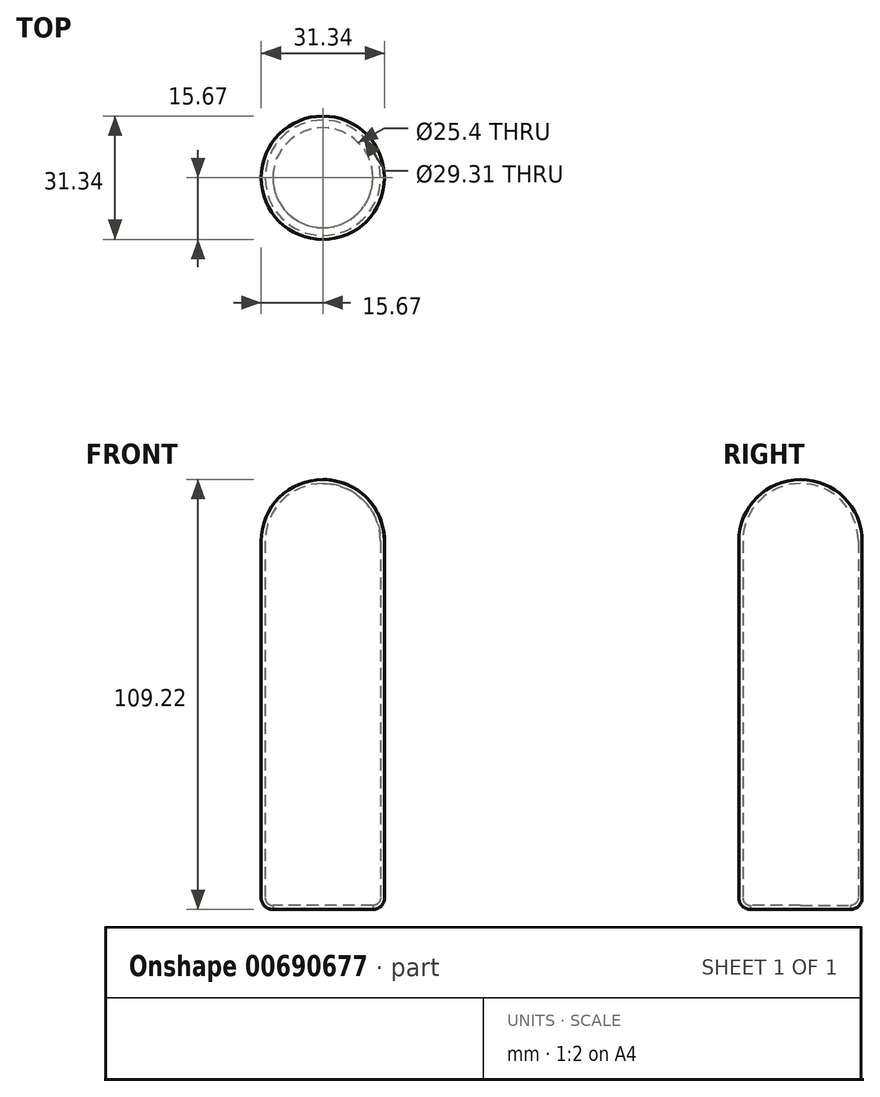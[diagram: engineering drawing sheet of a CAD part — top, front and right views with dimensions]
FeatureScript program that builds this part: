
annotation { "Feature Type Name" : "Feature", "Feature Type Description" : "" }
export const myFeature = defineFeature(function(context is Context, id is Id, definition is map)
    precondition{}
    {
        {
            var Q0;
            Q0=qCreatedBy(makeId("Front.planeOp"),FACE);
            var sketch = newSketch(context, id + "F0", { "sketchPlane" : qUnion([Q0])});
            skLineSegment(sketch, "E0", {"start": v(0, 0) * mm, "end": v(0, 109.22) * mm});
            skLineSegment(sketch, "E1", {"start": v(0, 0) * mm, "end": v(12.7, 0) * mm});
            skLineSegment(sketch, "E2", {"start": v(15.67, 2.97) * mm, "end": v(15.67, 93.55) * mm});
            skArc(sketch, "E3", {"start": v(15.67, 93.55) * mm, "mid": v(11.08, 104.63) * mm, "end": v(0, 109.22) * mm});
            skPoint(sketch, "E4.visualSharp", {"position": v(15.67, 0) * mm});
            skArc(sketch, "E4.filletArc", {"start": v(12.7, 0) * mm, "mid": v(14.8, 0.87) * mm, "end": v(15.67, 2.97) * mm});
            skSolve(sketch);
        }
        {
            var Q0;
            Q0 = qSketchRegion(id + "F0", true);
            var Q1;
            Q1=sQuery(id+"F0.wireOp",EDGE,"E0");
            revolve(context, id + "F1", {"surfaceOperationType" : NewSurfaceOperationType.NEW, "entities" : qUnion([Q0]), "axis" : qUnion([Q1]), "revolveType" : RevolveType.FULL});
        }
        {
            var Q0;
            Q0=makeQuery(id+"F1.opRevolve","SWEPT_FACE",FACE,{"disambiguationData":[OSD([sQuery(id+"F0.wireOp",EDGE,"E1")])]});
            shell(context, id + "F2", {"entities" : qUnion([Q0]), "thickness" : 1.02 * mm});
        }
    });
